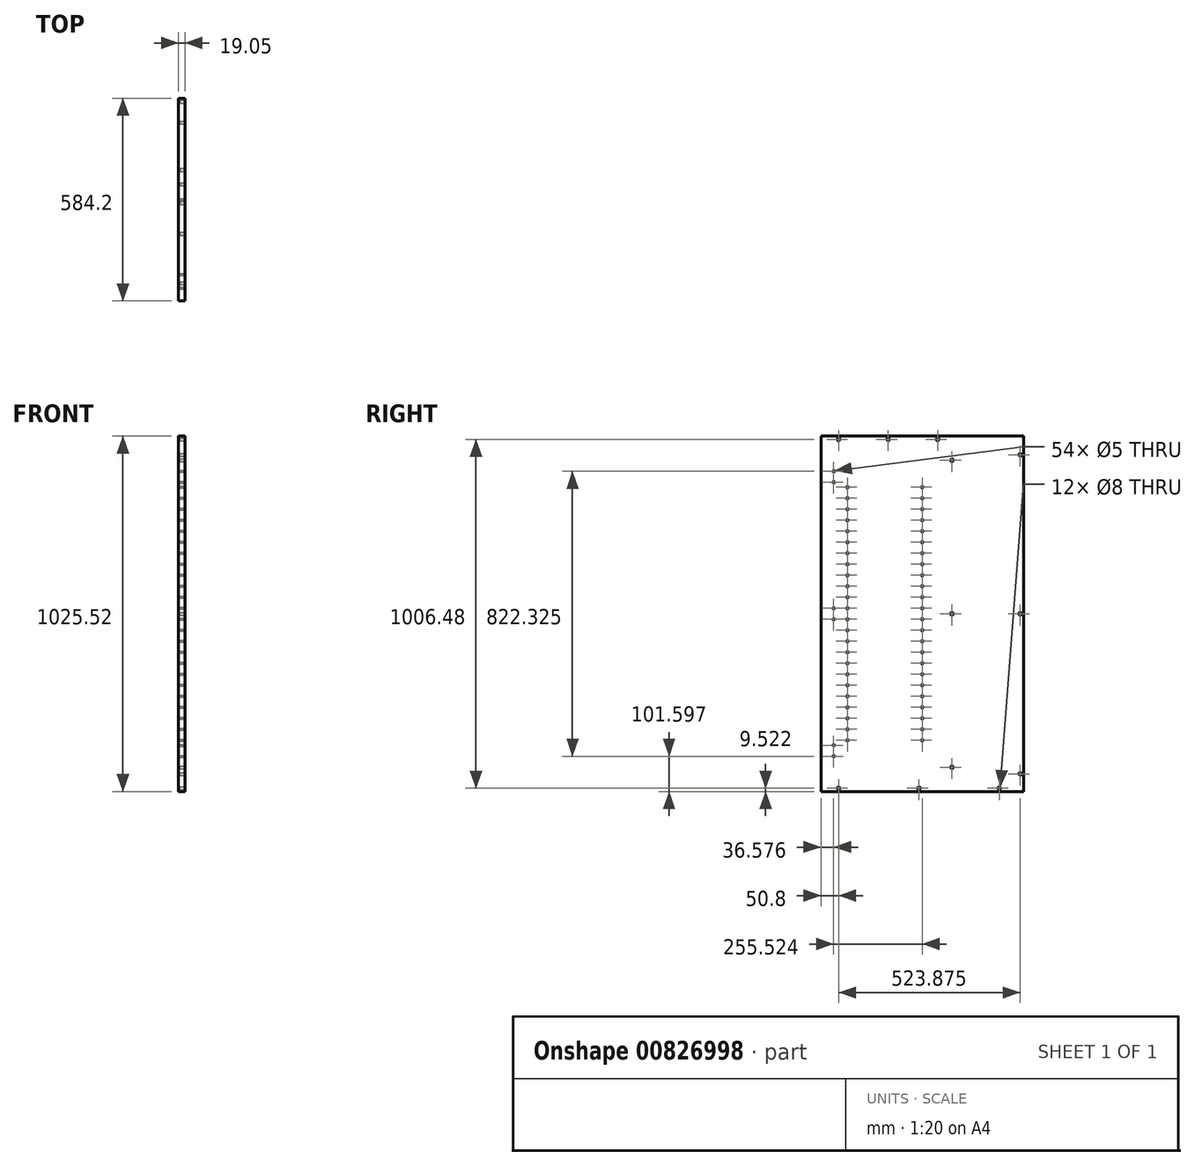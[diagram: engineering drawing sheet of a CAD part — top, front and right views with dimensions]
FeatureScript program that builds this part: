
annotation { "Feature Type Name" : "Feature", "Feature Type Description" : "" }
export const myFeature = defineFeature(function(context is Context, id is Id, definition is map)
    precondition{}
    {
        {
            var Q0;
            Q0=qCreatedBy(makeId("Right.planeOp"),FACE);
            var sketch = newSketch(context, id + "F0", { "sketchPlane" : qUnion([Q0])});
            skLineSegment(sketch, "E0.bottom", {"start": v(292.1, 512.76) * mm, "end": v(-292.1, 512.76) * mm});
            skLineSegment(sketch, "E0.top", {"start": v(292.1, -512.76) * mm, "end": v(-292.1, -512.76) * mm});
            skLineSegment(sketch, "E0.left", {"start": v(292.1, 512.76) * mm, "end": v(292.1, -512.76) * mm});
            skLineSegment(sketch, "E0.right", {"start": v(-292.1, 512.76) * mm, "end": v(-292.1, -512.76) * mm});
            skPoint(sketch, "E0.middle", {"position": v(0, 0) * mm});
            skSolve(sketch);
        }
        {
            var Q0;
            Q0=makeQuery(id+"F0.imprint","IMPRINT",FACE,{"disambiguationData":[TD([[makeQuery(id+"F0.imprint","IMPRINT",EDGE,{"derivedFrom":sQuery(id+"F0.wireOp",EDGE,"E0.bottom")}),1.0]])]});
            extrude(context, id + "F1", {"entities" : qUnion([Q0]), "depth" : 19.05 * mm, "offsetDistance" : 25.4 * mm});
        }
        {
            var Q0;
            Q0=makeQuery(id+"F1.opExtrude","CAP_FACE",FACE,{"disambiguationData":[OSD([sQuery(id+"F0.wireOp",EDGE,"E0.bottom"),sQuery(id+"F0.wireOp",EDGE,"E0.top"),sQuery(id+"F0.wireOp",EDGE,"E0.left"),sQuery(id+"F0.wireOp",EDGE,"E0.right")])],"isStart":false});
            var sketch = newSketch(context, id + "F2", { "sketchPlane" : qUnion([Q0])});
            skLineSegment(sketch, "E1.bottom", {"start": v(-292.1, -512.76) * mm, "end": v(273.05, -512.76) * mm});
            skLineSegment(sketch, "E1.top", {"start": v(-292.1, -493.71) * mm, "end": v(273.05, -493.71) * mm});
            skLineSegment(sketch, "E1.left", {"start": v(-292.1, -512.76) * mm, "end": v(-292.1, -493.71) * mm});
            skLineSegment(sketch, "E1.right", {"start": v(273.05, -512.76) * mm, "end": v(273.05, -493.71) * mm});
            skLineSegment(sketch, "E2", {"start": v(-292.1, -503.24) * mm, "end": v(-241.3, -503.24) * mm});
            skLineSegment(sketch, "E3", {"start": v(273.05, -503.24) * mm, "end": v(222.25, -503.24) * mm});
            skLineSegment(sketch, "E4", {"start": v(-9.53, -493.71) * mm, "end": v(-9.53, -512.76) * mm});
            skPoint(sketch, "E5", {"position": v(-241.3, -503.24) * mm});
            skPoint(sketch, "E6", {"position": v(-9.53, -503.24) * mm});
            skPoint(sketch, "E7", {"position": v(222.25, -503.24) * mm});
            skLineSegment(sketch, "E8", {"start": v(292.1, 512.76) * mm, "end": v(292.1, 509.59) * mm});
            skLineSegment(sketch, "E9.bottom", {"start": v(292.1, 509.59) * mm, "end": v(273.05, 509.59) * mm});
            skLineSegment(sketch, "E9.top", {"start": v(292.1, -512.76) * mm, "end": v(273.05, -512.76) * mm});
            skLineSegment(sketch, "E9.left", {"start": v(292.1, 509.59) * mm, "end": v(292.1, -512.76) * mm});
            skLineSegment(sketch, "E9.right", {"start": v(273.05, 509.59) * mm, "end": v(273.05, -512.76) * mm});
            skLineSegment(sketch, "E10", {"start": v(282.58, -512.76) * mm, "end": v(282.58, -461.96) * mm});
            skLineSegment(sketch, "E11", {"start": v(282.58, 509.59) * mm, "end": v(282.58, 458.79) * mm});
            skLineSegment(sketch, "E12", {"start": v(273.05, 0) * mm, "end": v(282.58, 0) * mm});
            skPoint(sketch, "E13", {"position": v(282.58, 0) * mm});
            skPoint(sketch, "E14", {"position": v(282.58, 458.79) * mm});
            skPoint(sketch, "E15", {"position": v(282.58, -461.96) * mm});
            skLineSegment(sketch, "E16.bottom", {"start": v(-292.1, 512.76) * mm, "end": v(95.25, 512.76) * mm});
            skLineSegment(sketch, "E16.top", {"start": v(-292.1, 493.71) * mm, "end": v(95.25, 493.71) * mm});
            skLineSegment(sketch, "E16.left", {"start": v(-292.1, 512.76) * mm, "end": v(-292.1, 493.71) * mm});
            skLineSegment(sketch, "E16.right", {"start": v(95.25, 512.76) * mm, "end": v(95.25, 493.71) * mm});
            skLineSegment(sketch, "E17", {"start": v(-292.1, 503.24) * mm, "end": v(-241.3, 503.24) * mm});
            skLineSegment(sketch, "E18", {"start": v(95.25, 503.24) * mm, "end": v(44.45, 503.24) * mm});
            skLineSegment(sketch, "E19", {"start": v(-98.43, 493.71) * mm, "end": v(-98.43, 512.76) * mm});
            skPoint(sketch, "E20", {"position": v(-241.3, 503.24) * mm});
            skPoint(sketch, "E21", {"position": v(-98.43, 503.24) * mm});
            skPoint(sketch, "E22", {"position": v(44.45, 503.24) * mm});
            skLineSegment(sketch, "E23.bottom", {"start": v(95.25, 493.71) * mm, "end": v(76.2, 493.71) * mm});
            skLineSegment(sketch, "E23.top", {"start": v(95.25, -493.71) * mm, "end": v(76.2, -493.71) * mm});
            skLineSegment(sketch, "E23.left", {"start": v(95.25, 493.71) * mm, "end": v(95.25, -493.71) * mm});
            skLineSegment(sketch, "E23.right", {"start": v(76.2, 493.71) * mm, "end": v(76.2, -493.71) * mm});
            skLineSegment(sketch, "E24", {"start": v(85.72, 493.71) * mm, "end": v(85.72, 442.91) * mm});
            skLineSegment(sketch, "E25", {"start": v(85.72, -493.71) * mm, "end": v(85.72, -442.91) * mm});
            skPoint(sketch, "E26", {"position": v(85.72, 442.91) * mm});
            skPoint(sketch, "E27", {"position": v(85.72, -442.91) * mm});
            skPoint(sketch, "E28", {"position": v(85.72, 0) * mm});
            skPoint(sketch, "E28.positionSnap0", {"position": v(95.25, 0) * mm});
            skSolve(sketch);
        }
        {
            var Q0;
            Q0=sQuery(id+"F2.wireOp",VERTEX,"E20");
            var Q1;
            Q1=sQuery(id+"F2.wireOp",VERTEX,"E21");
            var Q2;
            Q2=sQuery(id+"F2.wireOp",VERTEX,"E22");
            var Q3;
            Q3=sQuery(id+"F2.wireOp",VERTEX,"E26");
            var Q4;
            Q4=sQuery(id+"F2.wireOp",VERTEX,"E14");
            var Q5;
            Q5=sQuery(id+"F2.wireOp",VERTEX,"E13");
            var Q6;
            Q6=sQuery(id+"F2.wireOp",VERTEX,"E28");
            var Q7;
            Q7=sQuery(id+"F2.wireOp",VERTEX,"E15");
            var Q8;
            Q8=sQuery(id+"F2.wireOp",VERTEX,"E7");
            var Q9;
            Q9=sQuery(id+"F2.wireOp",VERTEX,"E27");
            var Q10;
            Q10=sQuery(id+"F2.wireOp",VERTEX,"E6");
            var Q11;
            Q11=sQuery(id+"F2.wireOp",VERTEX,"E5");
            var Q12;
            Q12=makeQuery(id+"F1.opExtrude","SWEPT_BODY",BODY,{"disambiguationData":[OSD([sQuery(id+"F0.wireOp",EDGE,"E0.bottom"),sQuery(id+"F0.wireOp",EDGE,"E0.top"),sQuery(id+"F0.wireOp",EDGE,"E0.left"),sQuery(id+"F0.wireOp",EDGE,"E0.right")])]});
            hole(context, id + "F3", {"style" : HoleStyle.SIMPLE, "endStyle" : HoleEndStyle.BLIND, "holeDiameter" : 8 * mm, "majorDiameter" : 6.35 * mm, "holeDepth" : 14.22 * mm, "isTappedThrough" : true, "tappedDepth" : 12.7 * mm, "tapClearance" : 3, "startFromSketch" : true, "locations" : qUnion([Q0, Q1, Q2, Q3, Q4, Q5, Q6, Q7, Q8, Q9, Q10, Q11]), "scope" : qUnion([Q12])});
        }
        {
            var Q0;
            Q0=makeQuery(id+"F1.opExtrude","CAP_FACE",FACE,{"disambiguationData":[OSD([sQuery(id+"F0.wireOp",EDGE,"E0.bottom"),sQuery(id+"F0.wireOp",EDGE,"E0.top"),sQuery(id+"F0.wireOp",EDGE,"E0.left"),sQuery(id+"F0.wireOp",EDGE,"E0.right")])],"isStart":false});
            var sketch = newSketch(context, id + "F4", { "sketchPlane" : qUnion([Q0])});
            skLineSegment(sketch, "E29", {"start": v(-292.1, 512.76) * mm, "end": v(-292.1, 411.16) * mm});
            skLineSegment(sketch, "E30", {"start": v(-292.1, 411.16) * mm, "end": v(-255.52, 411.16) * mm});
            skLineSegment(sketch, "E31", {"start": v(-292.1, -512.76) * mm, "end": v(-292.1, -411.16) * mm});
            skLineSegment(sketch, "E32", {"start": v(-292.1, -411.16) * mm, "end": v(-255.52, -411.16) * mm});
            skLineSegment(sketch, "E33", {"start": v(-255.52, -411.16) * mm, "end": v(-255.52, -379.41) * mm});
            skLineSegment(sketch, "E34", {"start": v(-255.52, 411.16) * mm, "end": v(-255.52, 379.41) * mm});
            skLineSegment(sketch, "E35", {"start": v(-292.1, 0) * mm, "end": v(-255.52, 0) * mm});
            skLineSegment(sketch, "E36", {"start": v(-255.52, 0) * mm, "end": v(-255.52, 15.88) * mm});
            skLineSegment(sketch, "E37", {"start": v(-255.52, 0) * mm, "end": v(-255.52, -15.88) * mm});
            skPoint(sketch, "E38", {"position": v(-255.52, 411.16) * mm});
            skPoint(sketch, "E39", {"position": v(-255.52, 379.41) * mm});
            skPoint(sketch, "E40", {"position": v(-255.52, 15.88) * mm});
            skPoint(sketch, "E41", {"position": v(-255.52, -15.88) * mm});
            skPoint(sketch, "E42", {"position": v(-255.52, -379.41) * mm});
            skPoint(sketch, "E43", {"position": v(-255.52, -411.16) * mm});
            skLineSegment(sketch, "E44", {"start": v(-292.1, 512.76) * mm, "end": v(-215.9, 512.76) * mm});
            skLineSegment(sketch, "E45", {"start": v(-215.9, 512.76) * mm, "end": v(-215.9, 365.19) * mm});
            skLineSegment(sketch, "E46", {"start": v(-292.1, 512.76) * mm, "end": v(0, 512.76) * mm});
            skLineSegment(sketch, "E47.bottom", {"start": v(-215.9, 365.19) * mm, "end": v(0, 365.19) * mm});
            skLineSegment(sketch, "E47.top", {"start": v(-215.9, 301.69) * mm, "end": v(0, 301.69) * mm});
            skLineSegment(sketch, "E47.left", {"start": v(-215.9, 365.19) * mm, "end": v(-215.9, 301.69) * mm});
            skLineSegment(sketch, "E47.right", {"start": v(0, 365.19) * mm, "end": v(0, 301.69) * mm});
            skLineSegment(sketch, "E48", {"start": v(-215.9, 301.69) * mm, "end": v(-215.9, 269.94) * mm});
            skLineSegment(sketch, "E49.bottom", {"start": v(-215.9, 269.94) * mm, "end": v(0, 269.94) * mm});
            skLineSegment(sketch, "E49.top", {"start": v(-215.9, 206.44) * mm, "end": v(0, 206.44) * mm});
            skLineSegment(sketch, "E49.left", {"start": v(-215.9, 269.94) * mm, "end": v(-215.9, 206.44) * mm});
            skLineSegment(sketch, "E49.right", {"start": v(0, 269.94) * mm, "end": v(0, 206.44) * mm});
            skLineSegment(sketch, "E50", {"start": v(-215.9, 206.44) * mm, "end": v(-215.9, 174.69) * mm});
            skLineSegment(sketch, "E51.bottom", {"start": v(-215.9, 174.69) * mm, "end": v(0, 174.69) * mm});
            skLineSegment(sketch, "E51.top", {"start": v(-215.9, 111.19) * mm, "end": v(0, 111.19) * mm});
            skLineSegment(sketch, "E51.left", {"start": v(-215.9, 174.69) * mm, "end": v(-215.9, 111.19) * mm});
            skLineSegment(sketch, "E51.right", {"start": v(0, 174.69) * mm, "end": v(0, 111.19) * mm});
            skLineSegment(sketch, "E52", {"start": v(-215.9, 111.19) * mm, "end": v(-215.9, 79.44) * mm});
            skLineSegment(sketch, "E53.bottom", {"start": v(-215.9, 79.44) * mm, "end": v(0, 79.44) * mm});
            skLineSegment(sketch, "E53.top", {"start": v(-215.9, 15.94) * mm, "end": v(0, 15.94) * mm});
            skLineSegment(sketch, "E53.left", {"start": v(-215.9, 79.44) * mm, "end": v(-215.9, 15.94) * mm});
            skLineSegment(sketch, "E53.right", {"start": v(0, 79.44) * mm, "end": v(0, 15.94) * mm});
            skLineSegment(sketch, "E54", {"start": v(-215.9, 15.94) * mm, "end": v(-215.9, -15.81) * mm});
            skLineSegment(sketch, "E55.bottom", {"start": v(-215.9, -15.81) * mm, "end": v(0, -15.81) * mm});
            skLineSegment(sketch, "E55.top", {"start": v(-215.9, -79.31) * mm, "end": v(0, -79.31) * mm});
            skLineSegment(sketch, "E55.left", {"start": v(-215.9, -15.81) * mm, "end": v(-215.9, -79.31) * mm});
            skLineSegment(sketch, "E55.right", {"start": v(0, -15.81) * mm, "end": v(0, -79.31) * mm});
            skLineSegment(sketch, "E56", {"start": v(-215.9, -79.31) * mm, "end": v(-215.9, -111.06) * mm});
            skLineSegment(sketch, "E57.bottom", {"start": v(-215.9, -111.06) * mm, "end": v(0, -111.06) * mm});
            skLineSegment(sketch, "E57.top", {"start": v(-215.9, -174.56) * mm, "end": v(0, -174.56) * mm});
            skLineSegment(sketch, "E57.left", {"start": v(-215.9, -111.06) * mm, "end": v(-215.9, -174.56) * mm});
            skLineSegment(sketch, "E57.right", {"start": v(0, -111.06) * mm, "end": v(0, -174.56) * mm});
            skLineSegment(sketch, "E58", {"start": v(-215.9, -174.56) * mm, "end": v(-215.9, -206.31) * mm});
            skLineSegment(sketch, "E59.bottom", {"start": v(-215.9, -206.31) * mm, "end": v(0, -206.31) * mm});
            skLineSegment(sketch, "E59.top", {"start": v(-215.9, -269.81) * mm, "end": v(0, -269.81) * mm});
            skLineSegment(sketch, "E59.left", {"start": v(-215.9, -206.31) * mm, "end": v(-215.9, -269.81) * mm});
            skLineSegment(sketch, "E59.right", {"start": v(0, -206.31) * mm, "end": v(0, -269.81) * mm});
            skLineSegment(sketch, "E60.bottom", {"start": v(-215.9, -269.81) * mm, "end": v(-215.9, -269.81) * mm});
            skLineSegment(sketch, "E61", {"start": v(-215.9, -269.81) * mm, "end": v(-215.9, -301.56) * mm});
            skLineSegment(sketch, "E62.bottom", {"start": v(-215.9, -301.56) * mm, "end": v(0, -301.56) * mm});
            skLineSegment(sketch, "E62.top", {"start": v(-215.9, -365.06) * mm, "end": v(0, -365.06) * mm});
            skLineSegment(sketch, "E62.left", {"start": v(-215.9, -301.56) * mm, "end": v(-215.9, -365.06) * mm});
            skLineSegment(sketch, "E62.right", {"start": v(0, -301.56) * mm, "end": v(0, -365.06) * mm});
            skPoint(sketch, "E63", {"position": v(-215.9, 365.19) * mm});
            skPoint(sketch, "E64", {"position": v(-215.9, 333.44) * mm});
            skPoint(sketch, "E65", {"position": v(-215.9, 301.69) * mm});
            skPoint(sketch, "E66", {"position": v(-215.9, 269.94) * mm});
            skPoint(sketch, "E67", {"position": v(-215.9, 238.19) * mm});
            skPoint(sketch, "E68", {"position": v(-215.9, 206.44) * mm});
            skPoint(sketch, "E69", {"position": v(-215.9, 174.69) * mm});
            skPoint(sketch, "E70", {"position": v(-215.9, 142.94) * mm});
            skPoint(sketch, "E71", {"position": v(-215.9, 111.19) * mm});
            skPoint(sketch, "E72", {"position": v(-215.9, 79.44) * mm});
            skPoint(sketch, "E73", {"position": v(-215.9, 47.69) * mm});
            skPoint(sketch, "E74", {"position": v(-215.9, 15.94) * mm});
            skPoint(sketch, "E75", {"position": v(-215.9, -15.81) * mm});
            skPoint(sketch, "E76", {"position": v(-215.9, -47.56) * mm});
            skPoint(sketch, "E77", {"position": v(-215.9, -79.31) * mm});
            skPoint(sketch, "E78", {"position": v(-215.9, -111.06) * mm});
            skPoint(sketch, "E79", {"position": v(-215.9, -142.81) * mm});
            skPoint(sketch, "E80", {"position": v(-215.9, -174.56) * mm});
            skPoint(sketch, "E81", {"position": v(-215.9, -206.31) * mm});
            skPoint(sketch, "E82", {"position": v(-215.9, -238.06) * mm});
            skPoint(sketch, "E83", {"position": v(-215.9, -269.81) * mm});
            skPoint(sketch, "E84", {"position": v(-215.9, -301.56) * mm});
            skPoint(sketch, "E85", {"position": v(-215.9, -333.31) * mm});
            skPoint(sketch, "E86", {"position": v(-215.9, -365.06) * mm});
            skPoint(sketch, "E87", {"position": v(0, -333.31) * mm});
            skPoint(sketch, "E88", {"position": v(0, -365.06) * mm});
            skPoint(sketch, "E89", {"position": v(0, -301.56) * mm});
            skPoint(sketch, "E90", {"position": v(0, -269.81) * mm});
            skPoint(sketch, "E91", {"position": v(0, -238.06) * mm});
            skPoint(sketch, "E92", {"position": v(0, -206.31) * mm});
            skPoint(sketch, "E93", {"position": v(0, -174.56) * mm});
            skPoint(sketch, "E94", {"position": v(0, -142.81) * mm});
            skPoint(sketch, "E95", {"position": v(0, -111.06) * mm});
            skPoint(sketch, "E96", {"position": v(0, -79.31) * mm});
            skPoint(sketch, "E97", {"position": v(0, -47.56) * mm});
            skPoint(sketch, "E98", {"position": v(0, -15.81) * mm});
            skPoint(sketch, "E99", {"position": v(0, 15.94) * mm});
            skPoint(sketch, "E100", {"position": v(0, 47.69) * mm});
            skPoint(sketch, "E101", {"position": v(0, 79.44) * mm});
            skPoint(sketch, "E102", {"position": v(0, 111.19) * mm});
            skPoint(sketch, "E103", {"position": v(0, 142.94) * mm});
            skPoint(sketch, "E104", {"position": v(0, 174.69) * mm});
            skPoint(sketch, "E105", {"position": v(0, 206.44) * mm});
            skPoint(sketch, "E106", {"position": v(0, 238.19) * mm});
            skPoint(sketch, "E107", {"position": v(0, 269.94) * mm});
            skPoint(sketch, "E108", {"position": v(0, 365.19) * mm});
            skPoint(sketch, "E109", {"position": v(0, 333.44) * mm});
            skPoint(sketch, "E110", {"position": v(0, 301.69) * mm});
            skSolve(sketch);
        }
        {
            var Q0;
            Q0=sQuery(id+"F4.wireOp",VERTEX,"E38");
            var Q1;
            Q1=sQuery(id+"F4.wireOp",VERTEX,"E39");
            var Q2;
            Q2=sQuery(id+"F4.wireOp",VERTEX,"E40");
            var Q3;
            Q3=sQuery(id+"F4.wireOp",VERTEX,"E41");
            var Q4;
            Q4=sQuery(id+"F4.wireOp",VERTEX,"E42");
            var Q5;
            Q5=sQuery(id+"F4.wireOp",VERTEX,"E43");
            var Q6;
            Q6=sQuery(id+"F4.wireOp",VERTEX,"E63");
            var Q7;
            Q7=sQuery(id+"F4.wireOp",VERTEX,"E65");
            var Q8;
            Q8=sQuery(id+"F4.wireOp",VERTEX,"E66");
            var Q9;
            Q9=sQuery(id+"F4.wireOp",VERTEX,"E68");
            var Q10;
            Q10=sQuery(id+"F4.wireOp",VERTEX,"E69");
            var Q11;
            Q11=sQuery(id+"F4.wireOp",VERTEX,"E71");
            var Q12;
            Q12=sQuery(id+"F4.wireOp",VERTEX,"E72");
            var Q13;
            Q13=sQuery(id+"F4.wireOp",VERTEX,"E73");
            var Q14;
            Q14=sQuery(id+"F4.wireOp",VERTEX,"E74");
            var Q15;
            Q15=sQuery(id+"F4.wireOp",VERTEX,"E75");
            var Q16;
            Q16=sQuery(id+"F4.wireOp",VERTEX,"E76");
            var Q17;
            Q17=sQuery(id+"F4.wireOp",VERTEX,"E77");
            var Q18;
            Q18=sQuery(id+"F4.wireOp",VERTEX,"E78");
            var Q19;
            Q19=sQuery(id+"F4.wireOp",VERTEX,"E79");
            var Q20;
            Q20=sQuery(id+"F4.wireOp",VERTEX,"E80");
            var Q21;
            Q21=sQuery(id+"F4.wireOp",VERTEX,"E81");
            var Q22;
            Q22=sQuery(id+"F4.wireOp",VERTEX,"E82");
            var Q23;
            Q23=sQuery(id+"F4.wireOp",VERTEX,"E83");
            var Q24;
            Q24=sQuery(id+"F4.wireOp",VERTEX,"E85");
            var Q25;
            Q25=sQuery(id+"F4.wireOp",VERTEX,"E86");
            var Q26;
            Q26=sQuery(id+"F4.wireOp",VERTEX,"E84");
            var Q27;
            Q27=sQuery(id+"F4.wireOp",VERTEX,"E88");
            var Q28;
            Q28=sQuery(id+"F4.wireOp",VERTEX,"E89");
            var Q29;
            Q29=sQuery(id+"F4.wireOp",VERTEX,"E90");
            var Q30;
            Q30=sQuery(id+"F4.wireOp",VERTEX,"E92");
            var Q31;
            Q31=sQuery(id+"F4.wireOp",VERTEX,"E93");
            var Q32;
            Q32=sQuery(id+"F4.wireOp",VERTEX,"E94");
            var Q33;
            Q33=sQuery(id+"F4.wireOp",VERTEX,"E95");
            var Q34;
            Q34=sQuery(id+"F4.wireOp",VERTEX,"E96");
            var Q35;
            Q35=sQuery(id+"F4.wireOp",VERTEX,"E98");
            var Q36;
            Q36=sQuery(id+"F4.wireOp",VERTEX,"E99");
            var Q37;
            Q37=sQuery(id+"F4.wireOp",VERTEX,"E101");
            var Q38;
            Q38=sQuery(id+"F4.wireOp",VERTEX,"E102");
            var Q39;
            Q39=sQuery(id+"F4.wireOp",VERTEX,"E104");
            var Q40;
            Q40=sQuery(id+"F4.wireOp",VERTEX,"E105");
            var Q41;
            Q41=sQuery(id+"F4.wireOp",VERTEX,"E107");
            var Q42;
            Q42=sQuery(id+"F4.wireOp",VERTEX,"E110");
            var Q43;
            Q43=sQuery(id+"F4.wireOp",VERTEX,"E108");
            var Q44;
            Q44=sQuery(id+"F4.wireOp",VERTEX,"E64");
            var Q45;
            Q45=sQuery(id+"F4.wireOp",VERTEX,"E109");
            var Q46;
            Q46=sQuery(id+"F4.wireOp",VERTEX,"E106");
            var Q47;
            Q47=sQuery(id+"F4.wireOp",VERTEX,"E67");
            var Q48;
            Q48=sQuery(id+"F4.wireOp",VERTEX,"E70");
            var Q49;
            Q49=sQuery(id+"F4.wireOp",VERTEX,"E103");
            var Q50;
            Q50=sQuery(id+"F4.wireOp",VERTEX,"E100");
            var Q51;
            Q51=sQuery(id+"F4.wireOp",VERTEX,"E97");
            var Q52;
            Q52=sQuery(id+"F4.wireOp",VERTEX,"E91");
            var Q53;
            Q53=sQuery(id+"F4.wireOp",VERTEX,"E87");
            var Q54;
            Q54=makeQuery(id+"F1.opExtrude","SWEPT_BODY",BODY,{"disambiguationData":[OSD([sQuery(id+"F0.wireOp",EDGE,"E0.bottom"),sQuery(id+"F0.wireOp",EDGE,"E0.top"),sQuery(id+"F0.wireOp",EDGE,"E0.left"),sQuery(id+"F0.wireOp",EDGE,"E0.right")])]});
            hole(context, id + "F5", {"style" : HoleStyle.SIMPLE, "endStyle" : HoleEndStyle.BLIND, "holeDiameter" : 5 * mm, "majorDiameter" : 6.35 * mm, "holeDepth" : 14.22 * mm, "isTappedThrough" : true, "tappedDepth" : 12.7 * mm, "tapClearance" : 3, "startFromSketch" : true, "locations" : qUnion([Q0, Q1, Q2, Q3, Q4, Q5, Q6, Q7, Q8, Q9, Q10, Q11, Q12, Q13, Q14, Q15, Q16, Q17, Q18, Q19, Q20, Q21, Q22, Q23, Q24, Q25, Q26, Q27, Q28, Q29, Q30, Q31, Q32, Q33, Q34, Q35, Q36, Q37, Q38, Q39, Q40, Q41, Q42, Q43, Q44, Q45, Q46, Q47, Q48, Q49, Q50, Q51, Q52, Q53]), "scope" : qUnion([Q54])});
        }
    });
